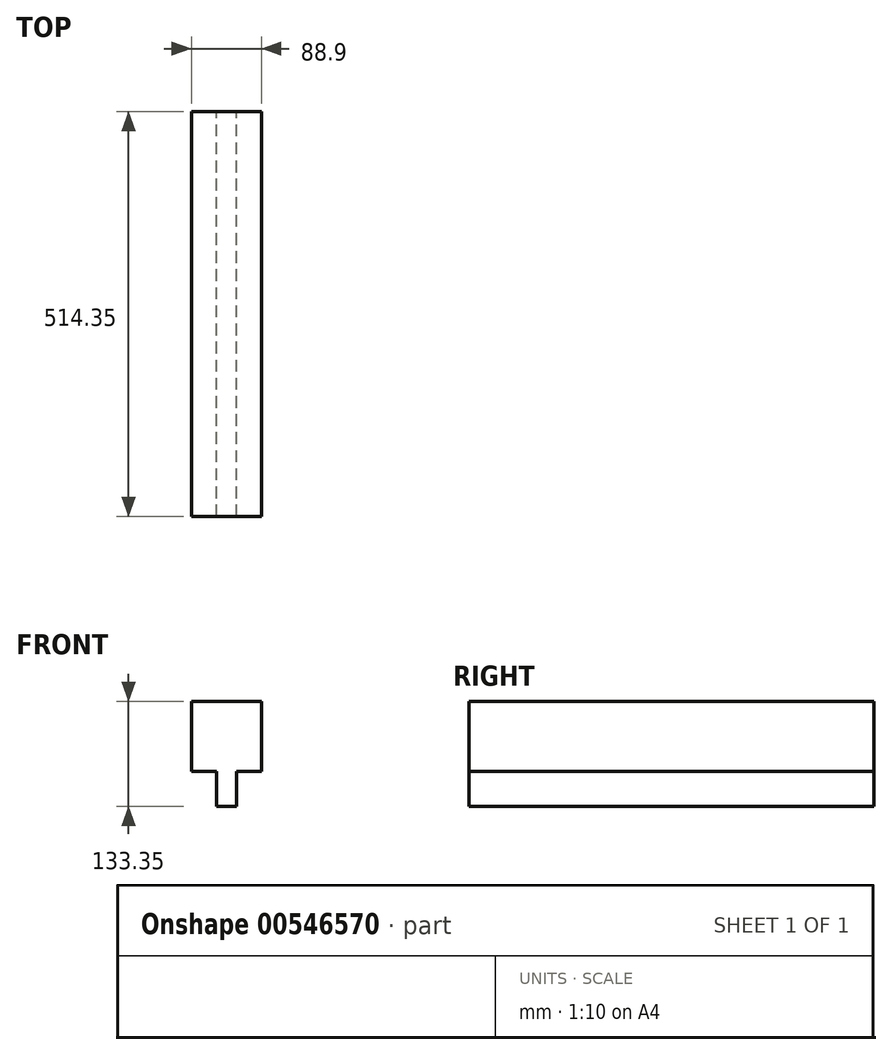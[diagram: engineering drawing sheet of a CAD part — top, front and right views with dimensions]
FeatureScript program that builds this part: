
annotation { "Feature Type Name" : "Feature", "Feature Type Description" : "" }
export const myFeature = defineFeature(function(context is Context, id is Id, definition is map)
    precondition{}
    {
        {
            var Q0;
            Q0=qCreatedBy(makeId("Front.planeOp"),FACE);
            var sketch = newSketch(context, id + "F0", { "sketchPlane" : qUnion([Q0])});
            skLineSegment(sketch, "E0.bottom", {"start": v(44.45, 44.45) * mm, "end": v(-44.45, 44.45) * mm});
            skLineSegment(sketch, "E0.top", {"start": v(44.45, -44.45) * mm, "end": v(12.7, -44.45) * mm});
            skLineSegment(sketch, "E0.left", {"start": v(44.45, 44.45) * mm, "end": v(44.45, -44.45) * mm});
            skLineSegment(sketch, "E0.right", {"start": v(-44.45, 44.45) * mm, "end": v(-44.45, -44.45) * mm});
            skPoint(sketch, "E0.middle", {"position": v(0, 0) * mm});
            skLineSegment(sketch, "E1.top", {"start": v(12.7, -88.9) * mm, "end": v(-12.7, -88.9) * mm});
            skLineSegment(sketch, "E1.left", {"start": v(12.7, -44.45) * mm, "end": v(12.7, -88.9) * mm});
            skLineSegment(sketch, "E1.right", {"start": v(-12.7, -44.45) * mm, "end": v(-12.7, -88.9) * mm});
            skPoint(sketch, "E1.middle", {"position": v(0, -46.3) * mm});
            skLineSegment(sketch, "E2.trimOffspring", {"start": v(-12.7, -44.45) * mm, "end": v(-44.45, -44.45) * mm});
            skPoint(sketch, "E1.bottom.end.orphan", {"position": v(-12.7, -3.7) * mm});
            skPoint(sketch, "E1.bottom.start.orphan", {"position": v(12.7, -3.7) * mm});
            skSolve(sketch);
        }
        {
            var Q0;
            Q0=makeQuery(id+"F0.imprint","IMPRINT",FACE,{"disambiguationData":[TD([[makeQuery(id+"F0.imprint","IMPRINT",EDGE,{"derivedFrom":sQuery(id+"F0.wireOp",EDGE,"E0.bottom")}),1.0]])]});
            extrude(context, id + "F1", {"entities" : qUnion([Q0]), "depth" : 514.35 * mm, "offsetDistance" : 25.4 * mm});
        }
    });
